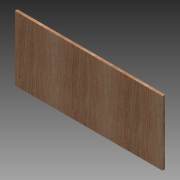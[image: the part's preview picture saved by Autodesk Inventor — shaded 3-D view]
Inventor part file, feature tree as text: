
AUTODESK INVENTOR PART (.ipt)
format: ipt  version: 2013 (Build 170138000, 138)  size: 90,624 bytes
history: native  units: in
note: dims shown in document units (in); Inventor stores cm internally (conversion verified against a paired STEP export)
features: extrude x1, sketch x1
ambient origin geometry x8: Origin, YZ Plane, XZ Plane, XY Plane, X Axis, Y Axis, Z Axis, Center Point
bodies: Solid1 (feature_tree)
feature tree (2):
  extrude  "Extrusion1"  Depth=28.0in
  sketch  "Sketch1"  dims[d0=12.25in d1=28.0in d2=0.5in d3=0.0in]
